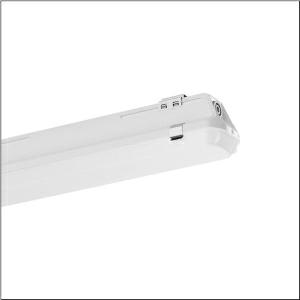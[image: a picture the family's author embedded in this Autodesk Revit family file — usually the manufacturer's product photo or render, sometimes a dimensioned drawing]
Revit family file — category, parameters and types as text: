
# Revit family: monsun_r__21_51fb10ml460k_f3f7
name_source: partatom
category: Lighting Fixtures
units: mm (PartAtom-declared; Revit-internal decimal feet)

## family parameters
Cut with Voids When Loaded = No
Host = Face
Light Source = No
Part Type = Normal
Room Calculation Point = No
Round Connector Dimension = Use Diameter
Shared = No

## types (1)
- --- (1 x LED, 6010 lm, 33.2 W, 4000K)
    Apparent Load = 33 VA
    CIE Flux Codes = 46 76 93 94 100
    Color Rendering = 80
    Color Temperature = 4000K
    Default Elevation = 1800 mm
    Description = Monsun® 21, damp-proof luminaire, chain hanger, primary optical cover: enclosure, of PMMA, light emission: direct distribution, primary light characteristic: symmetric, installation type: suspended mounting, surface-mounted, horizontal mounting, vertical mounting, LED, rated luminous flux: 6.010lm, luminous efficacy: 181lm/W, light colour: 840, colour temperature: 4000K, control gear: ON/OFF Multilumen, with terminal, 3-pole, max. 2.5mm², mains connection: 220..240V, AC, 50/60Hz, rated input power: 33W, housing, of glass-fibre reinforced plastic, uncoated, bright grey, incl. chain hanger, length: 1.299mm, width: 90mm, height: 88mm, clip for enclosure, of stainless steel (V2A), ceiling mounting element, of stainless steel (V2A), chain hanger, of stainless steel (V2A), protection rating (complete): IP66, insulation class (complete): insulation class I (protective earthing), certification: CE, ENEC, VDE, UKCA, protection symbol: D, impact resistance: IK04, permissible operating ambient temperature: -25..+35°C, standard: EN 50419, EN 60598-2-1, corresponds to IFS (International Featured Standards) requirements for safety and quality in the food industry, for indoor or canopied outdoor use, no direct snow, no direct sun, no direct rain, LABS conformity tested according to VDMA 24364:2018-05, contact your sales advisor before using the luminaires in applications with unclear chemical exposure, large temperature fluctuations or condensation-forming humidity, packaging unit: 1 piece
    Height = 88 mm
    Lamp = 1 x LED
    Lamp Light Flux = 6010 lm
    Lamp Power = 33.2 W
    Lamp count = 1
    Length = 1299 mm
    Luminous efficacy = 181 lm/W
    Manufacturer = Siteco
    ModVariant = No
    Model = 51FB10ML460K
    Mounting Place = Ceiling
    Mounting Type = Surface mounted
    Number of Poles = 1
    OnlyDefault = Yes
    Power Factor = 1
    Product Name = Monsun® 21
    Product group = damp-proof luminaire
    ProductGroupID = 301
    Protection Class = Protection class I
    Protection Degree = IP 66
    RLX_Detail_Level = 1
    RLX_Emergency_Light_Flux = 0 lm
    RLX_Emergency_Type = 0
    RLX_Emergency_Type_DB = No
    RlxData = <blob elided: 90857 chars, md5=2664b951>
    Socket = socket
    Standby Power = 0 W
    System Light Flux = 6010 lm
    System Power = 33 W
    Type Comments = factory setting: luminous flux: 100 % | (A | C | E) | 77 mA
    Type Image = l_1319656.jpg
    URL = http://relux.com
    VarID = @adj_051887
    Voltage = 0 V
    Weight = 0.00 kg
    Width = 90 mm

## geometry (parser evidence)
native form markers: Blend x4, Sweep x13
no freeform markers — native parametric forms only
